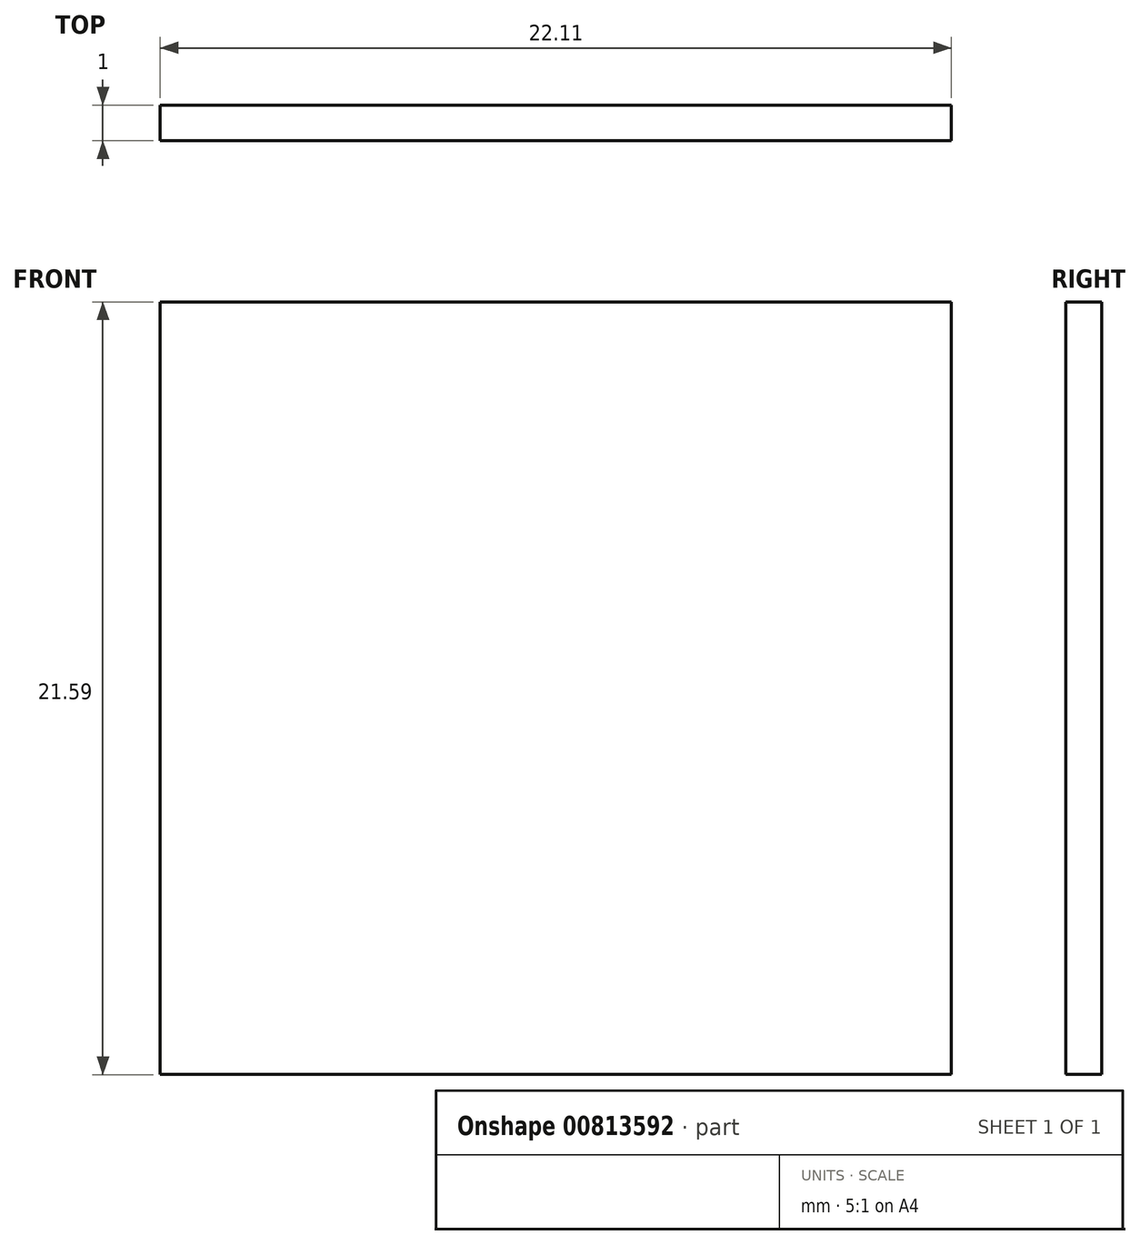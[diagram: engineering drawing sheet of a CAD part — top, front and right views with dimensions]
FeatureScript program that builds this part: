
annotation { "Feature Type Name" : "Feature", "Feature Type Description" : "" }
export const myFeature = defineFeature(function(context is Context, id is Id, definition is map)
    precondition{}
    {
        {
            var Q0;
            Q0=qCreatedBy(makeId("Front.planeOp"),FACE);
            var sketch = newSketch(context, id + "F0", { "sketchPlane" : qUnion([Q0])});
            skLineSegment(sketch, "E0.bottom", {"start": v(-32.55, 30.43) * mm, "end": v(-10.44, 30.43) * mm});
            skLineSegment(sketch, "E0.top", {"start": v(-32.55, 8.84) * mm, "end": v(-10.44, 8.84) * mm});
            skLineSegment(sketch, "E0.left", {"start": v(-32.55, 30.43) * mm, "end": v(-32.55, 8.84) * mm});
            skLineSegment(sketch, "E0.right", {"start": v(-10.44, 30.43) * mm, "end": v(-10.44, 8.84) * mm});
            skSolve(sketch);
        }
        {
            var Q0;
            Q0=makeQuery(id+"F0.imprint","IMPRINT",FACE,{"disambiguationData":[TD([[makeQuery(id+"F0.imprint","IMPRINT",EDGE,{"derivedFrom":sQuery(id+"F0.wireOp",EDGE,"E0.bottom")}),-1.0]])]});
            var Q1;
            Q1 = qSketchRegion(id + "F0", true);
            extrude(context, id + "F1", {"entities" : qUnion([Q0, Q1]), "depth" : 1 * mm, "offsetDistance" : 25 * mm});
        }
    });
